# Revit family: Lavatory-TOTO-Contemporary-Lloyd-LF930WCP
name_source: partatom
category: Plumbing Fixtures
revit_build: Autodesk Revit Architecture 2013 (Build: 20130531_2115(x64)
units: mm (PartAtom-declared; Revit-internal decimal feet)

## types (1)
- LF930WCP
    04 CSI = 22 42 16
    95 CSI = 15410
    ADA Compliant = No
    Assembly Code = D2010310
    Basin Depth = 26' - 0 3/8"
    Basin Diameter = 0' - 0"
    Basin Width = 13' - 0 3/4"
    Certifications = IAPMO(cUPC), State of Massachusetts , City of Los Angeles, and others
    Code Compliance = UPC, IPC, NSPC, NPC Canada, and others
    Cold Water Connection Radius = 0' - 0 1/2"
    Cold Water Connector = Cold Water Connection
    Color Availability = #01 Cotton, #03 Bone, #11 Colonial White, #12 Sedona Beige, #51 Ebony
    Default Elevation = 4' - 0"
    Depth = 1' - 7 5/8"
    Description = Lloyd® Wood Console Lavatory
    Finish = Vitreous China - TOTO - 01 Cotton
    Height = 2' - 10 3/8"
    Hot Water Connection Radius = 0' - 0 1/2"
    Hot Water Connector = Hot Water Connection
    Industry Standards = Meets and exceeds ASME A112.19.9M and CSA B45 series
    Manufacturer = TOTO USA, Inc.
    Manufacturer Fax = (770) 282-0002
    Material = Fireclay
    Model = LF930WCP
    Pipe Offset = 0' - 4"
    Sanitary Connector = Sanitary Connection
    Series = Lloyd
    Shipping Weight = 53.00 lb
    Spec Sheet URL = http://assets.totousa.com
    Stand = Wood - TOTO - Smooth - Black
    Style = Contemporary
    Subcategory = Lavatories
    Toto BIM Number = BM-00327
    URL = http://www.totousa.com
    Warranty = One Year Limited Warranty
    Warranty URL = http://www.totousa.com
    Waste Connection NPT Radius = 0' - 0 5/8"
    Width = 2' - 4 3/4"

## geometry (parser evidence)
native form markers: Blend x16, Sweep x4
no freeform markers — native parametric forms only
